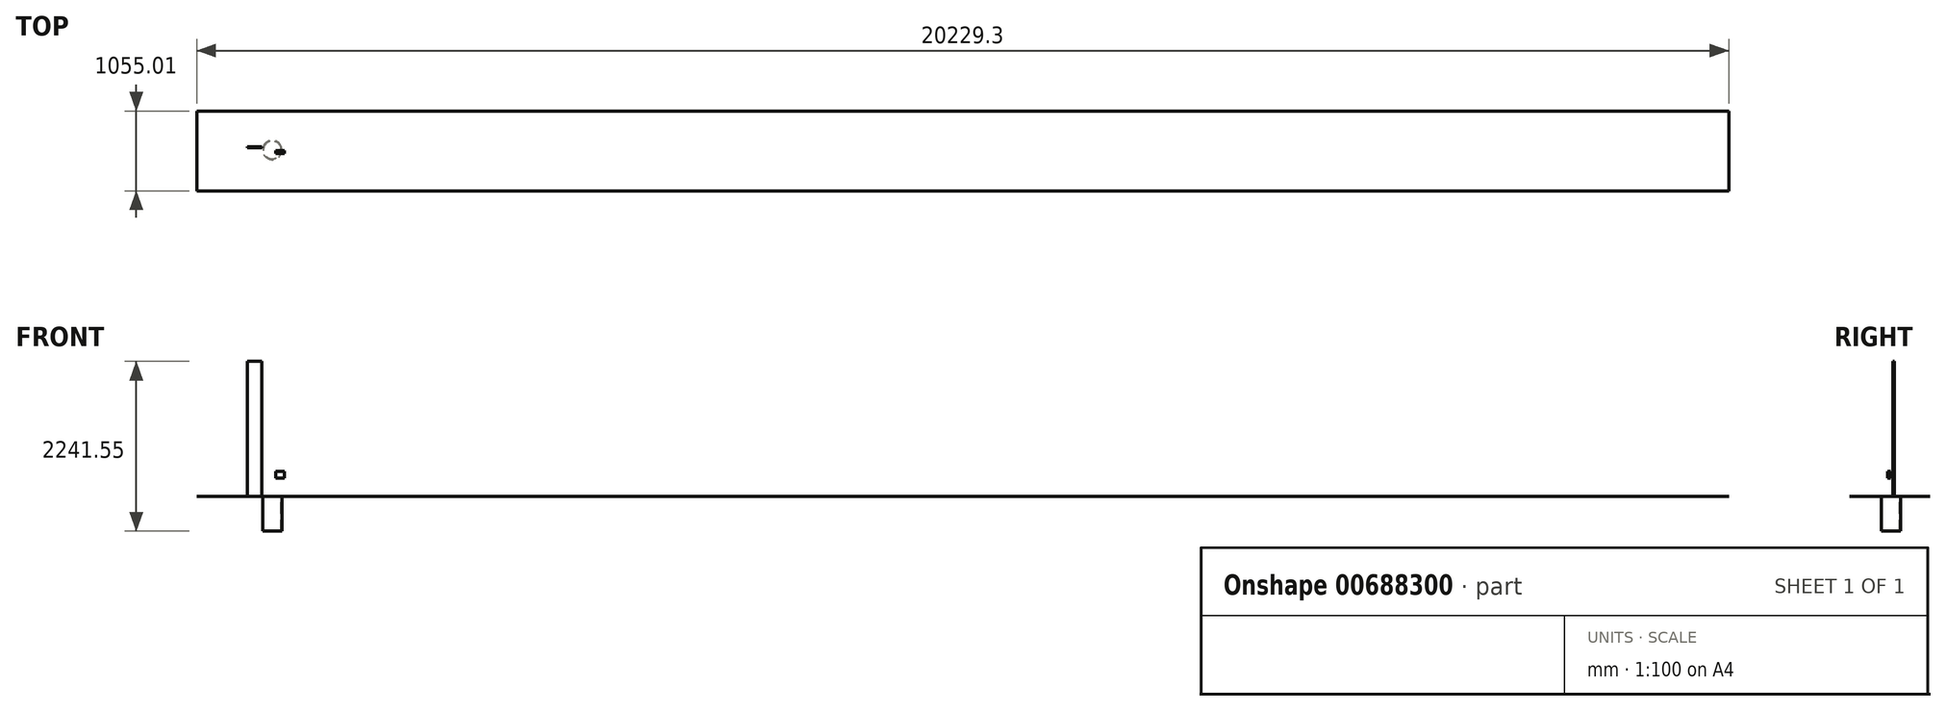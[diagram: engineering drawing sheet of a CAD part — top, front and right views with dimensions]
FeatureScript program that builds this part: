
annotation { "Feature Type Name" : "Feature", "Feature Type Description" : "" }
export const myFeature = defineFeature(function(context is Context, id is Id, definition is map)
    precondition{}
    {
        {
            var Q0;
            Q0=qCreatedBy(makeId("Top.planeOp"),FACE);
            var sketch = newSketch(context, id + "F0", { "sketchPlane" : qUnion([Q0])});
            skLineSegment(sketch, "E0", {"start": v(-9144, 0) * mm, "end": v(9144, 0) * mm});
            skSolve(sketch);
        }
        {
            var Q0;
            Q0=qCreatedBy(makeId("Top.planeOp"),FACE);
            var sketch = newSketch(context, id + "F1", { "sketchPlane" : qUnion([Q0])});
            skLineSegment(sketch, "E1.bottom", {"start": v(-9144, 0) * mm, "end": v(-9055.1, 0) * mm});
            skLineSegment(sketch, "E1.top", {"start": v(-9144, -88.9) * mm, "end": v(-9055.1, -88.9) * mm});
            skLineSegment(sketch, "E1.left", {"start": v(-9144, 0) * mm, "end": v(-9144, -88.9) * mm});
            skLineSegment(sketch, "E1.right", {"start": v(-9055.1, 0) * mm, "end": v(-9055.1, -88.9) * mm});
            skSolve(sketch);
        }
        {
            var Q0;
            Q0=makeQuery(id+"F1.imprint","IMPRINT",FACE,{"disambiguationData":[TD([[makeQuery(id+"F1.imprint","IMPRINT",EDGE,{"derivedFrom":sQuery(id+"F1.wireOp",EDGE,"E1.bottom")}),-1.0]])]});
            extrude(context, id + "F2", {"entities" : qUnion([Q0]), "depth" : 1981.2 * mm, "offsetDistance" : 25.4 * mm, "hasSecondDirection" : true, "secondDirectionOppositeDirection" : true, "secondDirectionDepth" : 457.2 * mm});
        }
        {
            var Q0;
            Q0=qCreatedBy(makeId("Top.planeOp"),FACE);
            var sketch = newSketch(context, id + "F3", { "sketchPlane" : qUnion([Q0])});
            skCircle(sketch, "E2", {"center": v(-9099.55, -44.45) * mm, "radius": 127 * mm});
            skLineSegment(sketch, "E3", {"start": v(-9099.55, -44.45) * mm, "end": v(-9144, -44.45) * mm});
            skLineSegment(sketch, "E4", {"start": v(-9099.55, -44.45) * mm, "end": v(-9099.55, 0) * mm});
            skCircle(sketch, "E5.0", {"center": v(-9099.55, -44.45) * mm, "radius": 117.47 * mm});
            skSolve(sketch);
        }
        {
            var Q0;
            Q0=makeQuery(id+"F3.imprint","IMPRINT",FACE,{"disambiguationData":[TD([[makeQuery(id+"F3.imprint","IMPRINT",EDGE,{"derivedFrom":sQuery(id+"F3.wireOp",EDGE,"E2")}),1.0]])]});
            var Q1;
            Q1=makeQuery(id+"F3.imprint","IMPRINT",FACE,{"disambiguationData":[TD([[makeQuery(id+"F3.imprint","IMPRINT",EDGE,{"derivedFrom":sQuery(id+"F3.wireOp",EDGE,"E5.0")}),-1.0]])]});
            extrude(context, id + "F4", {"entities" : qUnion([Q0, Q1]), "oppositeDirection" : true, "depth" : 457.2 * mm, "offsetDistance" : 25.4 * mm});
        }
        {
            var Q0;
            Q0=qCreatedBy(makeId("Front.planeOp"),FACE);
            var sketch = newSketch(context, id + "F5", { "sketchPlane" : qUnion([Q0])});
            skLineSegment(sketch, "E6", {"start": v(-9428.65, 0) * mm, "end": v(-9428.65, 1790.7) * mm});
            skLineSegment(sketch, "E7", {"start": v(-9238.15, 1790.7) * mm, "end": v(-9238.15, 0) * mm});
            skLineSegment(sketch, "E8", {"start": v(-9238.15, 0) * mm, "end": v(-9428.65, 0) * mm});
            skLineSegment(sketch, "E9", {"start": v(-9333.4, 0) * mm, "end": v(-9333.4, 1828.8) * mm});
            skLineSegment(sketch, "E10", {"start": v(-9428.65, 1790.7) * mm, "end": v(-9390.55, 1828.8) * mm});
            skLineSegment(sketch, "E11", {"start": v(-9390.55, 1828.8) * mm, "end": v(-9276.25, 1828.8) * mm});
            skLineSegment(sketch, "E12", {"start": v(-9276.25, 1828.8) * mm, "end": v(-9238.15, 1790.7) * mm});
            skSolve(sketch);
        }
        {
            var Q0;
            {var subQ2=sQuery(id+"F5.wireOp",EDGE,"E6");Q0=makeQuery(id+"F5.imprint","IMPRINT",FACE,{"disambiguationData":[TD([[makeQuery(id+"F5.imprint","IMPRINT",EDGE,{"derivedFrom":subQ2}),-1.0]])]});}
            var Q1;
            {var subQ4=sQuery(id+"F5.wireOp",EDGE,"E7");Q1=makeQuery(id+"F5.imprint","IMPRINT",FACE,{"disambiguationData":[TD([[makeQuery(id+"F5.imprint","IMPRINT",EDGE,{"derivedFrom":subQ4}),-1.0]])]});}
            extrude(context, id + "F6", {"entities" : qUnion([Q0, Q1]), "depth" : 15.88 * mm, "offsetDistance" : 25.4 * mm});
        }
        {
            var Q0;
            Q0=makeQuery(id+"F6.opExtrude","CAP_FACE",FACE,{"disambiguationData":[OSD([sQuery(id+"F5.wireOp",EDGE,"E6"),sQuery(id+"F5.wireOp",EDGE,"E7"),sQuery(id+"F5.wireOp",EDGE,"E8"),sQuery(id+"F5.wireOp",EDGE,"E10"),sQuery(id+"F5.wireOp",EDGE,"E11"),sQuery(id+"F5.wireOp",EDGE,"E12")])],"isStart":false});
            var sketch = newSketch(context, id + "F7", { "sketchPlane" : qUnion([Q0])});
            skLineSegment(sketch, "E13.bottom", {"start": v(-9428.65, 1784.35) * mm, "end": v(-9238.15, 1784.35) * mm});
            skLineSegment(sketch, "E13.top", {"start": v(-9428.65, 1828.8) * mm, "end": v(-9238.15, 1828.8) * mm});
            skLineSegment(sketch, "E13.left", {"start": v(-9428.65, 1784.35) * mm, "end": v(-9428.65, 1828.8) * mm});
            skLineSegment(sketch, "E13.right", {"start": v(-9238.15, 1784.35) * mm, "end": v(-9238.15, 1828.8) * mm});
            skSolve(sketch);
        }
        {
            var Q0;
            {var subQ2=sQuery(id+"F7.wireOp",EDGE,"E13.bottom");Q0=makeQuery(id+"F7.imprint","IMPRINT",FACE,{"disambiguationData":[TD([[makeQuery(id+"F7.imprint","IMPRINT",EDGE,{"derivedFrom":subQ2}),1.0]])]});}
            extrude(context, id + "F8", {"entities" : qUnion([Q0]), "operationType" : NewBodyOperationType.REMOVE, "oppositeDirection" : true, "depth" : 25.4 * mm, "offsetDistance" : 25.4 * mm});
        }
        {
            var Q0;
            Q0=makeQuery(id+"F2.opExtrude","SWEPT_FACE",FACE,{"disambiguationData":[OSD([sQuery(id+"F1.wireOp",EDGE,"E1.right")])]});
            var sketch = newSketch(context, id + "F9", { "sketchPlane" : qUnion([Q0])});
            skLineSegment(sketch, "E14.bottom", {"start": v(-88.9, 330.15) * mm, "end": v(-50.8, 330.15) * mm});
            skLineSegment(sketch, "E14.top", {"start": v(-88.9, 241.25) * mm, "end": v(-50.8, 241.25) * mm});
            skLineSegment(sketch, "E14.left", {"start": v(-88.9, 330.15) * mm, "end": v(-88.9, 241.25) * mm});
            skLineSegment(sketch, "E14.right", {"start": v(-50.8, 330.15) * mm, "end": v(-50.8, 241.25) * mm});
            skSolve(sketch);
        }
        {
            var Q0;
            Q0=makeQuery(id+"F9.imprint","IMPRINT",FACE,{"disambiguationData":[TD([[makeQuery(id+"F9.imprint","IMPRINT",EDGE,{"derivedFrom":sQuery(id+"F9.wireOp",EDGE,"E14.bottom")}),-1.0]])]});
            extrude(context, id + "F10", {"entities" : qUnion([Q0]), "depth" : ((10 * 12) - 3.5) * mm, "offsetDistance" : 25.4 * mm});
        }
        {
            var Q0;
            Q0=makeQuery(id+"F2.opExtrude","CAP_FACE",FACE,{"disambiguationData":[OSD([sQuery(id+"F1.wireOp",EDGE,"E1.bottom"),sQuery(id+"F1.wireOp",EDGE,"E1.top"),sQuery(id+"F1.wireOp",EDGE,"E1.left"),sQuery(id+"F1.wireOp",EDGE,"E1.right")])],"isStart":true});
            extrude(context, id + "F11", {"entities" : qUnion([Q0]), "operationType" : NewBodyOperationType.REMOVE, "endBound" : BoundingType.THROUGH_ALL, "oppositeDirection" : true, "depth" : 25.4 * mm, "offsetDistance" : 25.4 * mm});
        }
        {
            var Q0;
            Q0=qCreatedBy(makeId("Top.planeOp"),FACE);
            var sketch = newSketch(context, id + "F12", { "sketchPlane" : qUnion([Q0])});
            skLineSegment(sketch, "E15.bottom", {"start": v(-10097.22, 468.75) * mm, "end": v(10132.1, 468.75) * mm});
            skLineSegment(sketch, "E15.top", {"start": v(-10097.22, -586.26) * mm, "end": v(10132.1, -586.26) * mm});
            skLineSegment(sketch, "E15.left", {"start": v(-10097.22, 468.75) * mm, "end": v(-10097.22, -586.26) * mm});
            skLineSegment(sketch, "E15.right", {"start": v(10132.1, 468.75) * mm, "end": v(10132.1, -586.26) * mm});
            skSolve(sketch);
        }
        {
            var Q0;
            Q0=makeQuery(id+"F12.imprint","IMPRINT",FACE,{"disambiguationData":[TD([[makeQuery(id+"F12.imprint","IMPRINT",EDGE,{"derivedFrom":sQuery(id+"F12.wireOp",EDGE,"E15.bottom")}),-1.0]])]});
            extrude(context, id + "F13", {"entities" : qUnion([Q0]), "depth" : 0.03 * mm, "offsetDistance" : 25.4 * mm});
        }
    });
